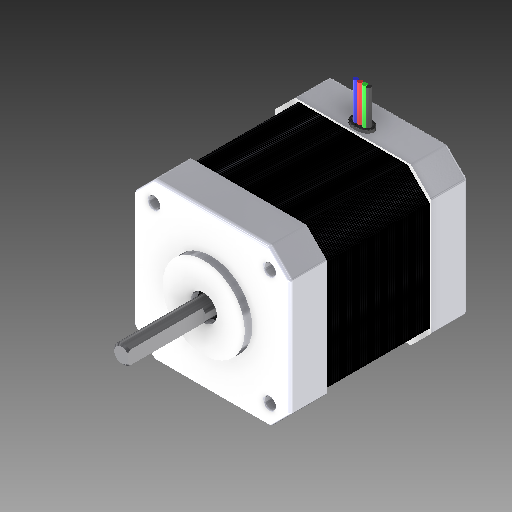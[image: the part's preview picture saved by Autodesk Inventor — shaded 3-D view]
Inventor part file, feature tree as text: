
AUTODESK INVENTOR PART (.ipt)
format: ipt  version: 2017 (Build 210142000, 142)  size: 1,188,864 bytes
history: native  units: mm
features: extrude x13, sketch x5, hole x4, fillet x4, chamfer x2, plane x1, pattern_linear x1, projected_geometry x1
ambient origin geometry x8: Origin, YZ Plane, XZ Plane, XY Plane, X Axis, Y Axis, Z Axis, Center Point
bodies: Solid1 (feature_tree)
feature tree (31):
  sketch  "Sketch1"  dims[d0=7.0mm d1=22.0mm]
  extrude  "Extrusion1"  Depth=22.0mm
  extrude  "Extrusion2"  Depth=31.0mm
  extrude  "Extrusion3"  Depth=3.0mm
  plane  "Work Plane2"
  extrude  "Extrusion7"  Depth=3.0mm
  extrude  "Extrusion8"  Depth=10.0mm
  chamfer  "Chamfer1"  Distance=42.0mm
  pattern_linear  "Rectangular Pattern2"  Spacing1=135.0deg  [1 undecoded]
  hole  "Hole1"  [1 undecoded]
  hole  "Hole2"  [1 undecoded]
  hole  "Hole3"  [1 undecoded]
  hole  "Hole4"  [1 undecoded]
  extrude  "Extrusion9"  Depth=10.0mm TaperAngle=0.0deg
  fillet  "Fillet1"  Radius=2.0mm
  fillet  "Fillet2"  Radius=48.0mm
  chamfer  "Chamfer2"  [1 undecoded]
  fillet  "Fillet3"  Radius=28.0mm
  sketch  "Sketch6"  dims[d10=3.0mm d11=3.0mm]
  extrude  "Extrusion10"  Depth=10.0mm
  fillet  "Fillet4"  Radius=1.0mm
  extrude  "Extrusion11"  Depth=10.0mm
  extrude  "Extrusion12"  Depth=10.0mm
  extrude  "Extrusion13"  Depth=10.0mm
  extrude  "Extrusion14"  Depth=10.0mm
  extrude  "Extrusion15"  Depth=10.0mm
  extrude  "Extrusion16"  Depth=10.0mm
  sketch  "Sketch4"  dims[d4=5.0mm d5=31.0mm]
  projected_geometry  "Projected Loop2"
  sketch  "Sketch5"  dims[d6=31.0mm d9=3.0mm]
  sketch  "Sketch11"  dims[d12=3.0mm d39=42.0mm d40=42.0mm d41=135.0deg d42=51.618795mm d43=51.618795mm d44=25.809398mm d45=25.809398mm d46=24.0mm d47=0.0mm d48=2.0mm d49=0.0mm d50=48.0mm d51=0.0mm d60=-10.0mm d126=28.0mm d127=0.0mm d128=1.0mm d129=1.0mm d130=1.0mm d131=1.0mm d132=0.5mm d134=0.5mm d135=0.5mm d136=0.5mm d137=0.5mm d138=1.0mm d139=1.0mm d140=0.5mm d141=0.0mm d145=0.125mm d146=2.0mm d147=45.0deg d148=560.0mm d150=0.5mm d151=10.0mm d152=10.0mm d153=6.0mm d154=6.0mm d155=4.0mm d156=2.0mm d157=90.0deg d158=3.0mm d159=0.0mm d160=10.0mm d161=10.0mm d162=6.0mm d163=6.0mm d164=4.0mm d165=2.0mm d166=90.0deg d167=3.0mm d168=0.0mm d169=10.0mm d170=10.0mm d171=6.0mm d172=6.0mm d173=4.0mm d174=2.0mm d175=90.0deg d176=3.0mm d177=0.0mm d178=10.0mm d179=10.0mm d180=6.0mm d181=6.0mm d182=4.0mm d183=2.0mm d184=90.0deg d185=3.0mm d186=0.0mm d187=48.0mm d188=0.0mm d189=47.0mm d190=0.0mm d191=1.0mm d192=1.0mm d193=0.5mm d194=2.0mm d195=45.0deg d196=0.5mm d197=1.2mm d198=40.0mm d200=1.2mm d201=10.0mm d203=10.0mm d205=2.5mm d206=2.5mm d207=1.0mm d208=0.0mm d209=0.3mm d210=10.0mm d211=0.0mm d212=10.0mm d213=0.0mm d214=10.0mm d215=0.0mm d216=10.0mm d217=0.0mm d218=0.2mm d219=5.0mm d220=0.0mm d221=0.0mm d225=20.0mm d226=0.0mm]
note: 6 required parameter values undecoded (feature->parameter linkage not recoverable at this tier; creation-order binding heuristic only, values carry confidence <= 0.55)
